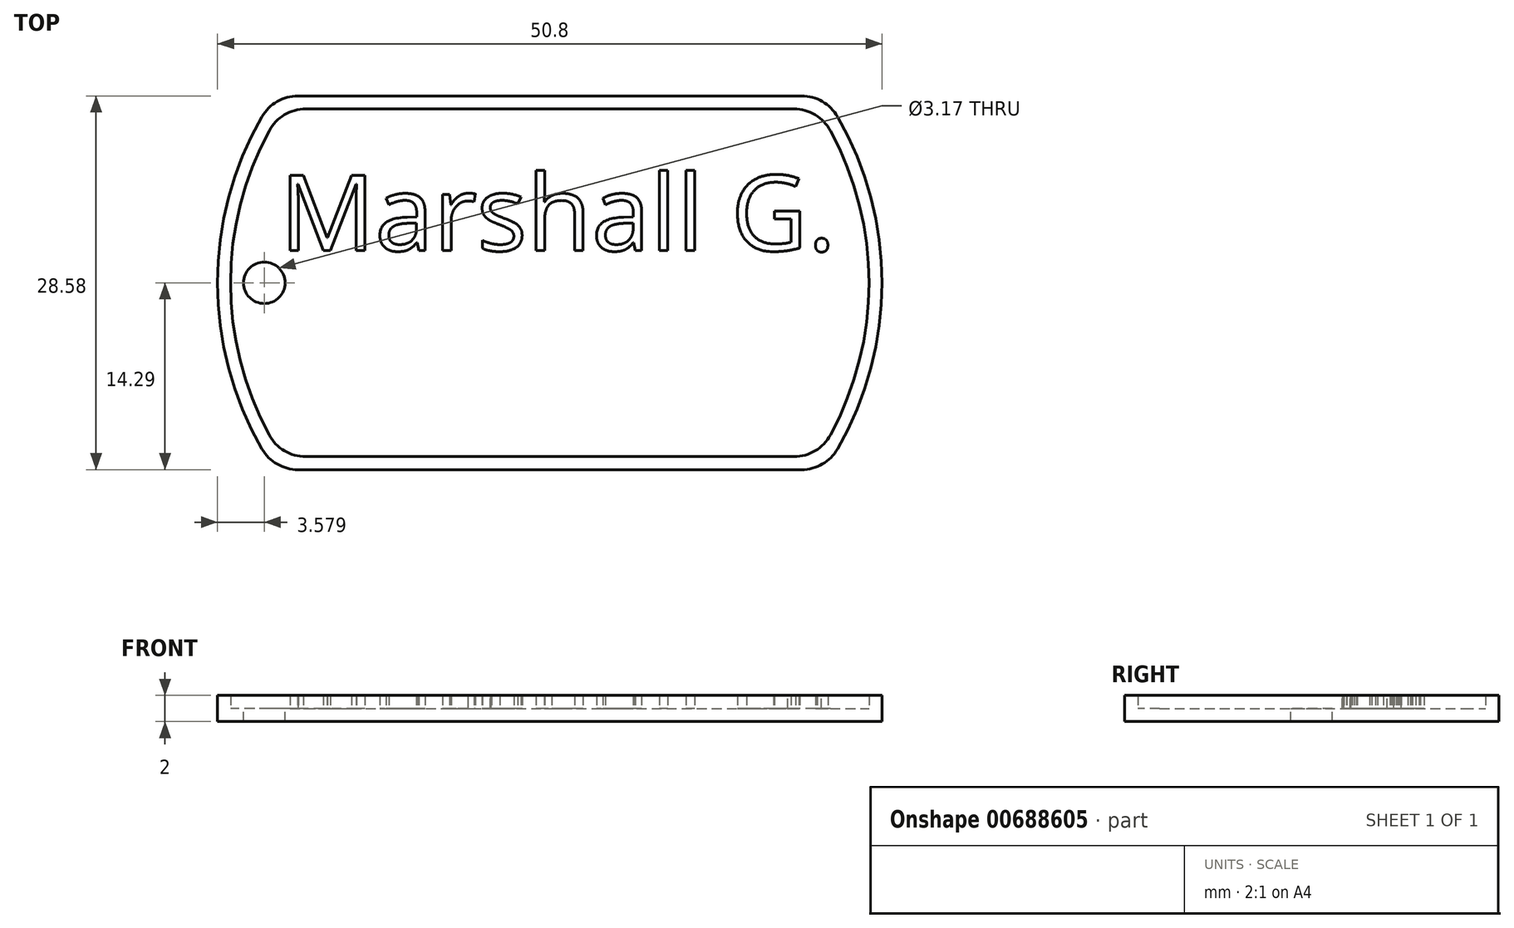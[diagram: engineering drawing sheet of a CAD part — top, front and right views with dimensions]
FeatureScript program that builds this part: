
annotation { "Feature Type Name" : "Feature", "Feature Type Description" : "" }
export const myFeature = defineFeature(function(context is Context, id is Id, definition is map)
    precondition{}
    {
        {
            var Q0;
            Q0=qCreatedBy(makeId("Top.planeOp"),FACE);
            var sketch = newSketch(context, id + "F0", { "sketchPlane" : qUnion([Q0])});
            skArc(sketch, "E0", {"start": v(-22, 12.7) * mm, "mid": v(-25.4, 0) * mm, "end": v(-22, -12.7) * mm});
            skLineSegment(sketch, "E1.top", {"start": v(-19.25, -14.29) * mm, "end": v(19.25, -14.29) * mm});
            skArc(sketch, "E2.trimOffspring", {"start": v(22, -12.7) * mm, "mid": v(25.4, 0) * mm, "end": v(22, 12.7) * mm});
            skLineSegment(sketch, "E3", {"start": v(-19.25, 14.29) * mm, "end": v(19.25, 14.29) * mm});
            skPoint(sketch, "E4.visualSharp", {"position": v(-21, 14.29) * mm});
            skArc(sketch, "E4.filletArc", {"start": v(-19.25, 14.29) * mm, "mid": v(-20.83, 13.86) * mm, "end": v(-22, 12.7) * mm});
            skPoint(sketch, "E5.visualSharp", {"position": v(21, 14.29) * mm});
            skArc(sketch, "E5.filletArc", {"start": v(22, 12.7) * mm, "mid": v(20.83, 13.86) * mm, "end": v(19.25, 14.29) * mm});
            skPoint(sketch, "E6.visualSharp", {"position": v(21, -14.29) * mm});
            skArc(sketch, "E6.filletArc", {"start": v(19.25, -14.29) * mm, "mid": v(20.83, -13.86) * mm, "end": v(22, -12.7) * mm});
            skPoint(sketch, "E7.visualSharp", {"position": v(-21, -14.29) * mm});
            skArc(sketch, "E7.filletArc", {"start": v(-22, -12.7) * mm, "mid": v(-20.83, -13.86) * mm, "end": v(-19.25, -14.29) * mm});
            skSolve(sketch);
        }
        {
            var Q0;
            Q0=makeQuery(id+"F0.imprint","IMPRINT",FACE,{"disambiguationData":[TD([[makeQuery(id+"F0.imprint","IMPRINT",EDGE,{"derivedFrom":sQuery(id+"F0.wireOp",EDGE,"E0")}),1.0]])]});
            extrude(context, id + "F1", {"entities" : qUnion([Q0]), "depth" : 1 * mm, "offsetDistance" : 25.4 * mm});
        }
        {
            var Q0;
            Q0=makeQuery(id+"F1.opExtrude","CAP_FACE",FACE,{"disambiguationData":[OSD([sQuery(id+"F0.wireOp",EDGE,"E0"),sQuery(id+"F0.wireOp",EDGE,"E1.top"),sQuery(id+"F0.wireOp",EDGE,"E2.trimOffspring"),sQuery(id+"F0.wireOp",EDGE,"E3"),sQuery(id+"F0.wireOp",EDGE,"E4.filletArc"),sQuery(id+"F0.wireOp",EDGE,"E5.filletArc"),sQuery(id+"F0.wireOp",EDGE,"E6.filletArc"),sQuery(id+"F0.wireOp",EDGE,"E7.filletArc")])],"isStart":false});
            var sketch = newSketch(context, id + "F2", { "sketchPlane" : qUnion([Q0])});
            skLineSegment(sketch, "E8.0", {"start": v(-18.66, 13.29) * mm, "end": v(18.66, 13.29) * mm});
            skArc(sketch, "E8.1", {"start": v(-21.45, 11.63) * mm, "mid": v(-24.4, 0) * mm, "end": v(-21.45, -11.63) * mm});
            skLineSegment(sketch, "E8.2", {"start": v(-18.66, -13.29) * mm, "end": v(18.66, -13.29) * mm});
            skArc(sketch, "E8.3", {"start": v(21.45, -11.63) * mm, "mid": v(24.4, 0) * mm, "end": v(21.45, 11.63) * mm});
            skPoint(sketch, "E9.visualSharp", {"position": v(-20.46, 13.29) * mm});
            skArc(sketch, "E9.filletArc", {"start": v(-18.66, 13.29) * mm, "mid": v(-20.29, 12.84) * mm, "end": v(-21.45, 11.63) * mm});
            skPoint(sketch, "E10.visualSharp", {"position": v(20.46, 13.29) * mm});
            skArc(sketch, "E10.filletArc", {"start": v(21.45, 11.63) * mm, "mid": v(20.29, 12.84) * mm, "end": v(18.66, 13.29) * mm});
            skPoint(sketch, "E11.visualSharp", {"position": v(20.46, -13.29) * mm});
            skArc(sketch, "E11.filletArc", {"start": v(18.66, -13.29) * mm, "mid": v(20.29, -12.84) * mm, "end": v(21.45, -11.63) * mm});
            skPoint(sketch, "E12.visualSharp", {"position": v(-20.46, -13.29) * mm});
            skArc(sketch, "E12.filletArc", {"start": v(-21.45, -11.63) * mm, "mid": v(-20.29, -12.84) * mm, "end": v(-18.66, -13.29) * mm});
            skLineSegment(sketch, "E13.0", {"start": v(-19.25, 14.29) * mm, "end": v(19.25, 14.29) * mm});
            skArc(sketch, "E13.1", {"start": v(-22, 12.7) * mm, "mid": v(-25.4, 0) * mm, "end": v(-22, -12.7) * mm});
            skLineSegment(sketch, "E13.2", {"start": v(-19.25, -14.29) * mm, "end": v(19.25, -14.29) * mm});
            skArc(sketch, "E13.3", {"start": v(22, -12.7) * mm, "mid": v(25.4, 0) * mm, "end": v(22, 12.7) * mm});
            skPoint(sketch, "E14.visualSharp", {"position": v(-21, -14.29) * mm});
            skArc(sketch, "E14.filletArc", {"start": v(-22, -12.7) * mm, "mid": v(-20.83, -13.86) * mm, "end": v(-19.25, -14.29) * mm});
            skPoint(sketch, "E15.visualSharp", {"position": v(21, -14.29) * mm});
            skArc(sketch, "E15.filletArc", {"start": v(19.25, -14.29) * mm, "mid": v(20.83, -13.86) * mm, "end": v(22, -12.7) * mm});
            skPoint(sketch, "E16.visualSharp", {"position": v(21, 14.29) * mm});
            skArc(sketch, "E16.filletArc", {"start": v(22, 12.7) * mm, "mid": v(20.83, 13.86) * mm, "end": v(19.25, 14.29) * mm});
            skPoint(sketch, "E17.visualSharp", {"position": v(-21, 14.29) * mm});
            skArc(sketch, "E17.filletArc", {"start": v(-19.25, 14.29) * mm, "mid": v(-20.83, 13.86) * mm, "end": v(-22, 12.7) * mm});
            skSolve(sketch);
        }
        {
            var Q0;
            Q0=makeQuery(id+"F2.imprint","IMPRINT",FACE,{"disambiguationData":[TD([[makeQuery(id+"F2.imprint","IMPRINT",EDGE,{"derivedFrom":sQuery(id+"F2.wireOp",EDGE,"E8.0")}),1.0]])]});
            extrude(context, id + "F3", {"entities" : qUnion([Q0]), "operationType" : NewBodyOperationType.ADD, "depth" : 1 * mm, "offsetDistance" : 25.4 * mm});
        }
        {
            var Q0;
            Q0=makeQuery(id+"F1.opExtrude","CAP_FACE",FACE,{"disambiguationData":[OSD([sQuery(id+"F0.wireOp",EDGE,"E0"),sQuery(id+"F0.wireOp",EDGE,"E1.top"),sQuery(id+"F0.wireOp",EDGE,"E2.trimOffspring"),sQuery(id+"F0.wireOp",EDGE,"E3"),sQuery(id+"F0.wireOp",EDGE,"E4.filletArc"),sQuery(id+"F0.wireOp",EDGE,"E5.filletArc"),sQuery(id+"F0.wireOp",EDGE,"E6.filletArc"),sQuery(id+"F0.wireOp",EDGE,"E7.filletArc")])],"isStart":false});
            var sketch = newSketch(context, id + "F4", { "sketchPlane" : qUnion([Q0])});
            skCircle(sketch, "E18", {"center": v(-21.82, 0) * mm, "radius": 1.59 * mm});
            skSolve(sketch);
        }
        {
            var Q0;
            Q0=makeQuery(id+"F4.imprint","IMPRINT",FACE,{"disambiguationData":[TD([[makeQuery(id+"F4.imprint","IMPRINT",EDGE,{"derivedFrom":sQuery(id+"F4.wireOp",EDGE,"E18")}),1.0]])]});
            extrude(context, id + "F5", {"entities" : qUnion([Q0]), "operationType" : NewBodyOperationType.REMOVE, "oppositeDirection" : true, "depth" : 1 * mm, "offsetDistance" : 25.4 * mm});
        }
        {
            var Q0;
            Q0=makeQuery(id+"F1.opExtrude","CAP_FACE",FACE,{"disambiguationData":[OSD([sQuery(id+"F0.wireOp",EDGE,"E0"),sQuery(id+"F0.wireOp",EDGE,"E1.top"),sQuery(id+"F0.wireOp",EDGE,"E2.trimOffspring"),sQuery(id+"F0.wireOp",EDGE,"E3"),sQuery(id+"F0.wireOp",EDGE,"E4.filletArc"),sQuery(id+"F0.wireOp",EDGE,"E5.filletArc"),sQuery(id+"F0.wireOp",EDGE,"E6.filletArc"),sQuery(id+"F0.wireOp",EDGE,"E7.filletArc")])],"isStart":false});
            var sketch = newSketch(context, id + "F6", { "sketchPlane" : qUnion([Q0])});
            skText(sketch, "E19", { "text": "Marshall G.", "fontName": "OpenSans-Regular.ttf"});
            const initialGuessF6  = {"E19": [-0.02063, 0.00246, 1, 0, 0.0058]};
            skSetInitialGuess(sketch, initialGuessF6);
            skSolve(sketch);
        }
        {
            var Q0;
            Q0 = qSketchRegion(id + "F6", true);
            extrude(context, id + "F7", {"entities" : qUnion([Q0]), "operationType" : NewBodyOperationType.ADD, "depth" : 1 * mm, "offsetDistance" : 25.4 * mm});
        }
    });
